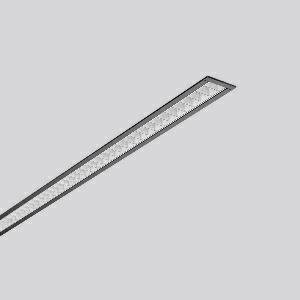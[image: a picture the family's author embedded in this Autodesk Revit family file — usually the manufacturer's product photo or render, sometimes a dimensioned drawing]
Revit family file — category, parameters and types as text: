
# Revit family: less_is_more_27_312179_003_76_47ff
name_source: partatom
category: Lighting Fixtures
units: mm (PartAtom-declared; Revit-internal decimal feet)

## family parameters
Cut with Voids When Loaded = No
Host = Face
Light Source = No
Part Type = Normal
Room Calculation Point = No
Round Connector Dimension = Use Diameter
Shared = No

## types (1)
- LESS IS MORE 27 (1 x LED Modul 830, 3500 lm, 3000)
    Apparent Load = 43 VA
    CIE Flux Codes = 90 99 100 100 100
    Color Rendering = 80
    Color Temperature = 3000
    Default Elevation = 1800 mm
    Description = Series: LESS IS MORE 27
Recessed ceiling and wall luminaire with slim design. Housing: extruded aluminium profile, powder-coated. End cap aluminium powder-coated. High polish aluminium micro grid. Perfect for office areas (RUG < 19) and environments with computer screens in accordance with EN 12464-1. Suitable for Recessed ceiling mounting, wall (recessed). External driver with connecting cable. 
Colour: deep black, matt (RAL 9005)
Length: 1514 mm
Width: 38 mm
Height: 2 mm
Cut-out length: 1506 mm
Cut-out width: 30 mm
Recess height: 45-60 mm
Luminaire: recess height: 37 mm
Lamp: LED
Socket: without socket
Colour temperature: 3000K
Colour rendering index (CRI): 82
System power: 43 W
Rated luminous flux: 3500 lm
Luminous efficiency: 81 lm/W
Control gear: Voltage converter, DALI dim.
Protection class: II
Type of protection: IP 20
    Height = 0 mm  [stored 0 ft]
    Lamp = 1 x LED Modul 830
    Lamp Light Flux = 3500 lm
    Lamp count = 1
    Length = 1514 mm
    Lifetime = 50000 h
    Luminous efficacy = 81 lm/W
    Manufacturer = RZB
    ModVariant = No
    Model = 312179.003.76
    Mounting Place = Ceiling, Wall
    Mounting Type = Recessed
    Number of Poles = 1
    OnlyDefault = Yes
    Power Factor = 1
    Product Name = LESS IS MORE 27
    Product group = Recessed LED linear luminaires
    ProductGroupID = 407
    Protection Class = Protection class II
    Protection Degree = IP 20
    RLX_Detail_Level = 1
    RLX_Emergency_Light_Flux = 0 lm
    RLX_Emergency_Type = 0
    RLX_Emergency_Type_DB = No
    RlxData = <blob elided: 29993 chars, md5=78514c52>
    Socket = socket
    Standby Power = 0 W
    System Light Flux = 3500 lm
    System Power = 43 W
    Type Comments = Product without accessories
    Type Image = 312177.003.jpg
    URL = http://relux.com
    VarID = ---
    Voltage = 230 V
    Voltage Range = 220-240 V
    Weight = 0.00 kg
    Width = 38 mm

note: [stored X ft] marks values corroborated as IEEE doubles in the binary element streams (Revit-internal decimal feet)

## geometry (parser evidence)
native form markers: Blend x4, Sweep x10
no freeform markers — native parametric forms only
